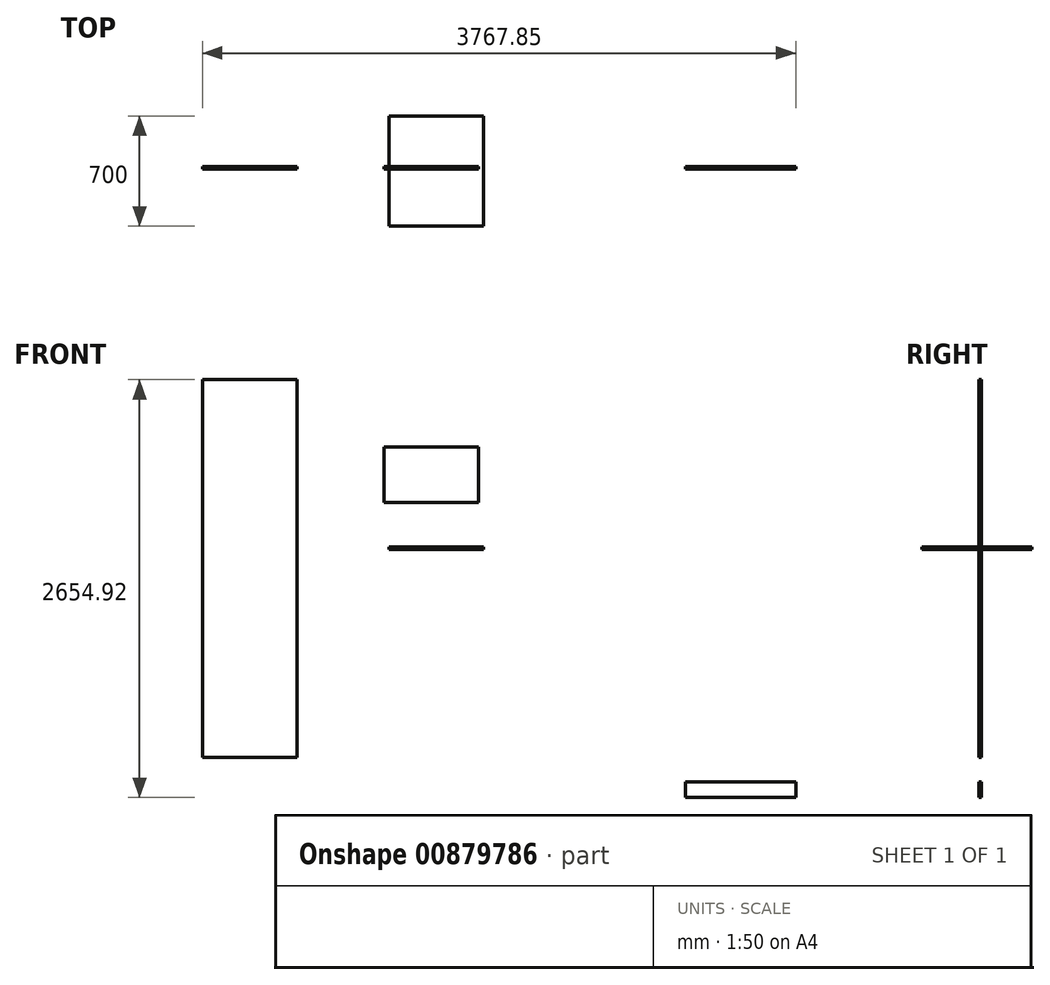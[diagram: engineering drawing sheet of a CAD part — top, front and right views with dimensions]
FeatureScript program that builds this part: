
annotation { "Feature Type Name" : "Feature", "Feature Type Description" : "" }
export const myFeature = defineFeature(function(context is Context, id is Id, definition is map)
    precondition{}
    {
        {
            var Q0;
            Q0=qCreatedBy(makeId("Front.planeOp"),FACE);
            var sketch = newSketch(context, id + "F0", { "sketchPlane" : qUnion([Q0])});
            skLineSegment(sketch, "E0.bottom", {"start": v(-1365.33, 1078.75) * mm, "end": v(-765.33, 1078.75) * mm});
            skLineSegment(sketch, "E0.top", {"start": v(-1365.33, -1321.25) * mm, "end": v(-765.33, -1321.25) * mm});
            skLineSegment(sketch, "E0.left", {"start": v(-1365.33, 1078.75) * mm, "end": v(-1365.33, -1321.25) * mm});
            skLineSegment(sketch, "E0.right", {"start": v(-765.33, 1078.75) * mm, "end": v(-765.33, -1321.25) * mm});
            skSolve(sketch);
        }
        {
            var Q0;
            Q0=makeQuery(id+"F0.imprint","IMPRINT",FACE,{"disambiguationData":[TD([[makeQuery(id+"F0.imprint","IMPRINT",EDGE,{"derivedFrom":sQuery(id+"F0.wireOp",EDGE,"E0.bottom")}),-1.0]])]});
            extrude(context, id + "F1", {"entities" : qUnion([Q0]), "depth" : 15 * mm, "offsetDistance" : 25 * mm});
        }
        {
            var Q0;
            Q0=qCreatedBy(makeId("Top.planeOp"),FACE);
            var sketch = newSketch(context, id + "F2", { "sketchPlane" : qUnion([Q0])});
            skLineSegment(sketch, "E1.bottom", {"start": v(418.1, 321.66) * mm, "end": v(-181.9, 321.66) * mm});
            skLineSegment(sketch, "E1.top", {"start": v(418.1, -378.34) * mm, "end": v(-181.9, -378.34) * mm});
            skLineSegment(sketch, "E1.left", {"start": v(418.1, 321.66) * mm, "end": v(418.1, -378.34) * mm});
            skLineSegment(sketch, "E1.right", {"start": v(-181.9, 321.66) * mm, "end": v(-181.9, -378.34) * mm});
            skSolve(sketch);
        }
        {
            var Q0;
            Q0=makeQuery(id+"F2.imprint","IMPRINT",FACE,{"disambiguationData":[TD([[makeQuery(id+"F2.imprint","IMPRINT",EDGE,{"derivedFrom":sQuery(id+"F2.wireOp",EDGE,"E1.bottom")}),1.0]])]});
            extrude(context, id + "F3", {"entities" : qUnion([Q0]), "depth" : 15 * mm, "offsetDistance" : 25 * mm});
        }
        {
            var Q0;
            Q0=qCreatedBy(makeId("Front.planeOp"),FACE);
            var sketch = newSketch(context, id + "F4", { "sketchPlane" : qUnion([Q0])});
            skLineSegment(sketch, "E2.bottom", {"start": v(1702.52, -1476.17) * mm, "end": v(2402.52, -1476.17) * mm});
            skLineSegment(sketch, "E2.top", {"start": v(1702.52, -1576.17) * mm, "end": v(2402.52, -1576.17) * mm});
            skLineSegment(sketch, "E2.left", {"start": v(1702.52, -1476.17) * mm, "end": v(1702.52, -1576.17) * mm});
            skLineSegment(sketch, "E2.right", {"start": v(2402.52, -1476.17) * mm, "end": v(2402.52, -1576.17) * mm});
            skSolve(sketch);
        }
        {
            var Q0;
            Q0=makeQuery(id+"F4.imprint","IMPRINT",FACE,{"disambiguationData":[TD([[makeQuery(id+"F4.imprint","IMPRINT",EDGE,{"derivedFrom":sQuery(id+"F4.wireOp",EDGE,"E2.bottom")}),-1.0]])]});
            extrude(context, id + "F5", {"entities" : qUnion([Q0]), "depth" : 15 * mm, "offsetDistance" : 25 * mm});
        }
        {
            var Q0;
            Q0=qCreatedBy(makeId("Front.planeOp"),FACE);
            var sketch = newSketch(context, id + "F6", { "sketchPlane" : qUnion([Q0])});
            skLineSegment(sketch, "E3.bottom", {"start": v(-212.44, 649.9) * mm, "end": v(387.56, 649.9) * mm});
            skLineSegment(sketch, "E3.top", {"start": v(-212.44, 299.9) * mm, "end": v(387.56, 299.9) * mm});
            skLineSegment(sketch, "E3.left", {"start": v(-212.44, 649.9) * mm, "end": v(-212.44, 299.9) * mm});
            skLineSegment(sketch, "E3.right", {"start": v(387.56, 649.9) * mm, "end": v(387.56, 299.9) * mm});
            skSolve(sketch);
        }
        {
            var Q0;
            Q0=makeQuery(id+"F6.imprint","IMPRINT",FACE,{"disambiguationData":[TD([[makeQuery(id+"F6.imprint","IMPRINT",EDGE,{"derivedFrom":sQuery(id+"F6.wireOp",EDGE,"E3.bottom")}),-1.0]])]});
            extrude(context, id + "F7", {"entities" : qUnion([Q0]), "depth" : 15 * mm, "offsetDistance" : 25 * mm});
        }
    });
